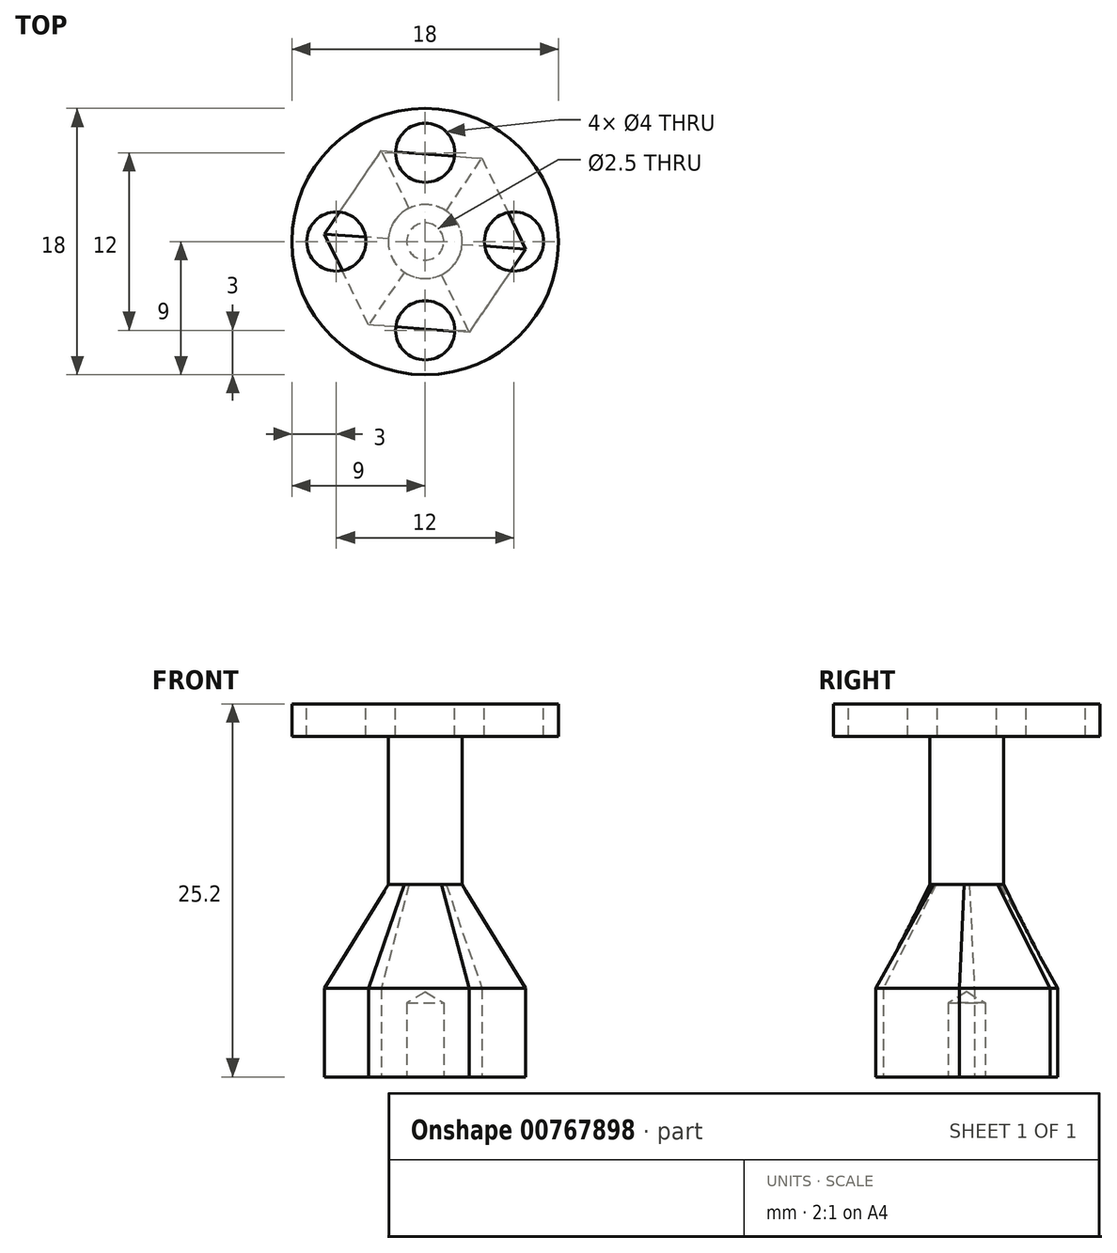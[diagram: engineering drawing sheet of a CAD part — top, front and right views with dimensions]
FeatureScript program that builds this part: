
annotation { "Feature Type Name" : "Feature", "Feature Type Description" : "" }
export const myFeature = defineFeature(function(context is Context, id is Id, definition is map)
    precondition{}
    {
        {
            var Q0;
            Q0=qCreatedBy(makeId("Top.planeOp"),FACE);
            var sketch = newSketch(context, id + "F0", { "sketchPlane" : qUnion([Q0])});
            skCircle(sketch, "E0.cCircle", {"center": v(0, 0) * mm, "radius": 5.9 * mm, "construction": true});
            skLineSegment(sketch, "E0.0", {"start": v(6.8, -0.5) * mm, "end": v(2.96, -6.14) * mm});
            skLineSegment(sketch, "E0.1", {"start": v(2.96, -6.14) * mm, "end": v(-3.83, -5.63) * mm});
            skLineSegment(sketch, "E0.2", {"start": v(-3.83, -5.63) * mm, "end": v(-6.8, 0.5) * mm});
            skLineSegment(sketch, "E0.3", {"start": v(-6.8, 0.5) * mm, "end": v(-2.96, 6.14) * mm});
            skLineSegment(sketch, "E0.4", {"start": v(-2.96, 6.14) * mm, "end": v(3.83, 5.63) * mm});
            skLineSegment(sketch, "E0.5", {"start": v(3.83, 5.63) * mm, "end": v(6.8, -0.5) * mm});
            skPoint(sketch, "E0.0.midPoint", {"position": v(4.88, -3.32) * mm});
            skSolve(sketch);
        }
        {
            var Q0;
            Q0 = qSketchRegion(id + "F0", true);
            extrude(context, id + "F1", {"entities" : qUnion([Q0]), "depth" : 6 * mm, "offsetDistance" : 25 * mm});
        }
        {
            var Q0;
            Q0=makeQuery(id+"F1.opExtrude","CAP_FACE",FACE,{"disambiguationData":[OSD([sQuery(id+"F0.wireOp",EDGE,"E0.0"),sQuery(id+"F0.wireOp",EDGE,"E0.1"),sQuery(id+"F0.wireOp",EDGE,"E0.2"),sQuery(id+"F0.wireOp",EDGE,"E0.3"),sQuery(id+"F0.wireOp",EDGE,"E0.4"),sQuery(id+"F0.wireOp",EDGE,"E0.5")])],"isStart":false});
            var sketch = newSketch(context, id + "F2", { "sketchPlane" : qUnion([Q0])});
            skCircle(sketch, "E1", {"center": v(0, 0) * mm, "radius": 2.5 * mm});
            skSolve(sketch);
        }
        {
            var Q0;
            Q0 = qSketchRegion(id + "F2", true);
            extrude(context, id + "F3", {"entities" : qUnion([Q0]), "operationType" : NewBodyOperationType.ADD, "depth" : 17 * mm, "offsetDistance" : 25 * mm});
        }
        {
            var Q0;
            Q0=makeQuery(id+"F3.opExtrude","CAP_FACE",FACE,{"disambiguationData":[OSD([sQuery(id+"F2.wireOp",EDGE,"E1")])],"isStart":false});
            var sketch = newSketch(context, id + "F4", { "sketchPlane" : qUnion([Q0])});
            skCircle(sketch, "E2", {"center": v(0, 0) * mm, "radius": 9 * mm});
            skSolve(sketch);
        }
        {
            var Q0;
            Q0 = qSketchRegion(id + "F4", true);
            extrude(context, id + "F5", {"entities" : qUnion([Q0]), "operationType" : NewBodyOperationType.ADD, "depth" : 2.2 * mm, "offsetDistance" : 25 * mm});
        }
        {
            var Q0;
            Q0=makeQuery(id+"F5.opExtrude","CAP_FACE",FACE,{"disambiguationData":[OSD([sQuery(id+"F4.wireOp",EDGE,"E2")])],"isStart":false});
            var sketch = newSketch(context, id + "F6", { "sketchPlane" : qUnion([Q0])});
            skCircle(sketch, "E3.0", {"center": v(6, 0) * mm, "radius": 2 * mm});
            skCircle(sketch, "E4.0", {"center": v(0, -6) * mm, "radius": 2 * mm});
            skCircle(sketch, "E5.0", {"center": v(-6, 0) * mm, "radius": 2 * mm});
            skCircle(sketch, "E6.0", {"center": v(0, 6) * mm, "radius": 2 * mm});
            skCircle(sketch, "E7.0", {"center": v(0, 0) * mm, "radius": 8.9 * mm});
            skCircle(sketch, "E8.0.0", {"center": v(0, 0) * mm, "radius": 2.8 * mm});
            skLineSegment(sketch, "E9", {"start": v(0, 6) * mm, "end": v(0, -6) * mm, "construction": true});
            skLineSegment(sketch, "E10", {"start": v(-6, 0) * mm, "end": v(6, 0) * mm, "construction": true});
            skSolve(sketch);
        }
        {
            var Q0;
            Q0=makeQuery(id+"F6.imprint","IMPRINT",FACE,{"disambiguationData":[TD([[makeQuery(id+"F6.imprint","IMPRINT",EDGE,{"derivedFrom":sQuery(id+"F6.wireOp",EDGE,"E5.0")}),1.0]])]});
            var Q1;
            Q1=makeQuery(id+"F6.imprint","IMPRINT",FACE,{"disambiguationData":[TD([[makeQuery(id+"F6.imprint","IMPRINT",EDGE,{"derivedFrom":sQuery(id+"F6.wireOp",EDGE,"E6.0")}),1.0]])]});
            var Q2;
            Q2=makeQuery(id+"F6.imprint","IMPRINT",FACE,{"disambiguationData":[TD([[makeQuery(id+"F6.imprint","IMPRINT",EDGE,{"derivedFrom":sQuery(id+"F6.wireOp",EDGE,"E3.0")}),1.0]])]});
            var Q3;
            Q3=makeQuery(id+"F6.imprint","IMPRINT",FACE,{"disambiguationData":[TD([[makeQuery(id+"F6.imprint","IMPRINT",EDGE,{"derivedFrom":sQuery(id+"F6.wireOp",EDGE,"E4.0")}),1.0]])]});
            extrude(context, id + "F7", {"entities" : qUnion([Q0, Q1, Q2, Q3]), "operationType" : NewBodyOperationType.REMOVE, "oppositeDirection" : true, "depth" : 3 * mm, "offsetDistance" : 25 * mm});
        }
        {
            var Q0;
            Q0=makeQuery(id+"F1.opExtrude","CAP_FACE",FACE,{"disambiguationData":[OSD([sQuery(id+"F0.wireOp",EDGE,"E0.0"),sQuery(id+"F0.wireOp",EDGE,"E0.1"),sQuery(id+"F0.wireOp",EDGE,"E0.2"),sQuery(id+"F0.wireOp",EDGE,"E0.3"),sQuery(id+"F0.wireOp",EDGE,"E0.4"),sQuery(id+"F0.wireOp",EDGE,"E0.5")])],"isStart":true});
            var sketch = newSketch(context, id + "F8", { "sketchPlane" : qUnion([Q0])});
            skPoint(sketch, "E11", {"position": v(0, 0) * mm});
            skSolve(sketch);
        }
        {
            var Q0;
            Q0=sQuery(id+"F8.wireOp",VERTEX,"E11");
            var Q1;
            Q1=makeQuery(id+"F1.opExtrude","SWEPT_BODY",BODY,{"disambiguationData":[OSD([sQuery(id+"F0.wireOp",EDGE,"E0.0"),sQuery(id+"F0.wireOp",EDGE,"E0.1"),sQuery(id+"F0.wireOp",EDGE,"E0.2"),sQuery(id+"F0.wireOp",EDGE,"E0.3"),sQuery(id+"F0.wireOp",EDGE,"E0.4"),sQuery(id+"F0.wireOp",EDGE,"E0.5")])]});
            hole(context, id + "F9", {"style" : HoleStyle.SIMPLE, "endStyle" : HoleEndStyle.BLIND, "standardTappedOrClearance" : lookupTablePath({ "standard" : "ISO", "engagement" : "75%", "pitch" : "0.5 mm", "size" : "M3", "type" : "Tapped" }), "standardBlindInLast" : lookupTablePath({ "standard" : "ISO", "engagement" : "75%", "pitch" : "0.5 mm", "size" : "M3", "type" : "Tapped" }), "holeDiameter" : 2.5 * mm, "majorDiameter" : 3 * mm, "showTappedDepth" : true, "holeDepth" : 5 * mm, "isTappedThrough" : true, "tappedDepth" : 3.5 * mm, "tapClearance" : 3, "locations" : qUnion([Q0]), "scope" : qUnion([Q1])});
        }
        {
            var Q0;
            Q0=qCreatedBy(makeId("Top.planeOp"),FACE);
            cPlane(context, id + "F10", {"entities" : qUnion([Q0]), "cplaneType" : CPlaneType.OFFSET, "offset" : 13 * mm, "width" : 150 * mm, "height" : 150 * mm});
        }
        {
            var Q0;
            Q0=qCreatedBy(id+"F10.planeOp",FACE);
            var sketch = newSketch(context, id + "F11", { "sketchPlane" : qUnion([Q0])});
            skCircle(sketch, "E12.0", {"center": v(0, 0) * mm, "radius": 2.5 * mm});
            skSolve(sketch);
        }
        {
            var Q0;
            Q0=makeQuery(id+"F1.opExtrude","CAP_FACE",FACE,{"disambiguationData":[OSD([sQuery(id+"F0.wireOp",EDGE,"E0.0"),sQuery(id+"F0.wireOp",EDGE,"E0.1"),sQuery(id+"F0.wireOp",EDGE,"E0.2"),sQuery(id+"F0.wireOp",EDGE,"E0.3"),sQuery(id+"F0.wireOp",EDGE,"E0.4"),sQuery(id+"F0.wireOp",EDGE,"E0.5")])],"isStart":false});
            var sketch = newSketch(context, id + "F12", { "sketchPlane" : qUnion([Q0])});
            skLineSegment(sketch, "E13.0", {"start": v(3.83, 5.63) * mm, "end": v(6.8, -0.5) * mm});
            skLineSegment(sketch, "E14.0", {"start": v(-2.96, 6.14) * mm, "end": v(3.83, 5.63) * mm});
            skLineSegment(sketch, "E15.0", {"start": v(-6.8, 0.5) * mm, "end": v(-2.96, 6.14) * mm});
            skLineSegment(sketch, "E16.0", {"start": v(-3.83, -5.63) * mm, "end": v(-6.8, 0.5) * mm});
            skLineSegment(sketch, "E17.0", {"start": v(6.8, -0.5) * mm, "end": v(2.96, -6.14) * mm});
            skLineSegment(sketch, "E18.0", {"start": v(2.96, -6.14) * mm, "end": v(-3.83, -5.63) * mm});
            skSolve(sketch);
        }
        {
            var Q0;
            Q0 = qSketchRegion(id + "F11", true);
            var Q1;
            Q1 = qSketchRegion(id + "F12", true);
            loft(context, id + "F13", {"operationType" : NewBodyOperationType.ADD, "sheetProfilesArray" : [{ "sheetProfileEntities" : qUnion([Q0]) }, { "sheetProfileEntities" : qUnion([Q1]) }]});
        }
    });
